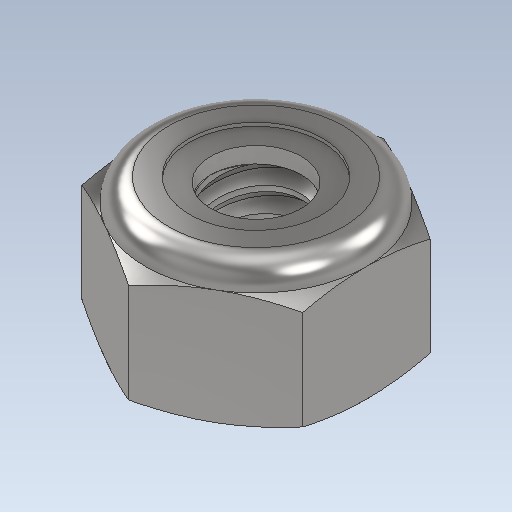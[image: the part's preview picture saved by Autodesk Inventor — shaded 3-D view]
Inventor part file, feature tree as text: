
AUTODESK INVENTOR PART (.ipt)
format: ipt  version: 2023 (Build 270158000, 158)  size: 305,152 bytes
history: native  units: in
note: dims shown in document units (in); Inventor stores cm internally (conversion verified against a paired STEP export)
features: other x1, revolve x1
ambient origin geometry x8: Origin, YZ Plane, XZ Plane, XY Plane, X Axis, Y Axis, Z Axis, Center Point
bodies: Solid1 (feature_tree), Solid2 (feature_tree)
feature tree (2):
  other  "Cut-Revolve4"
  revolve  "Revolve2"  [1 undecoded]
note: 1 required parameter value undecoded (feature->parameter linkage not recoverable at this tier; creation-order binding heuristic only, values carry confidence <= 0.55)
